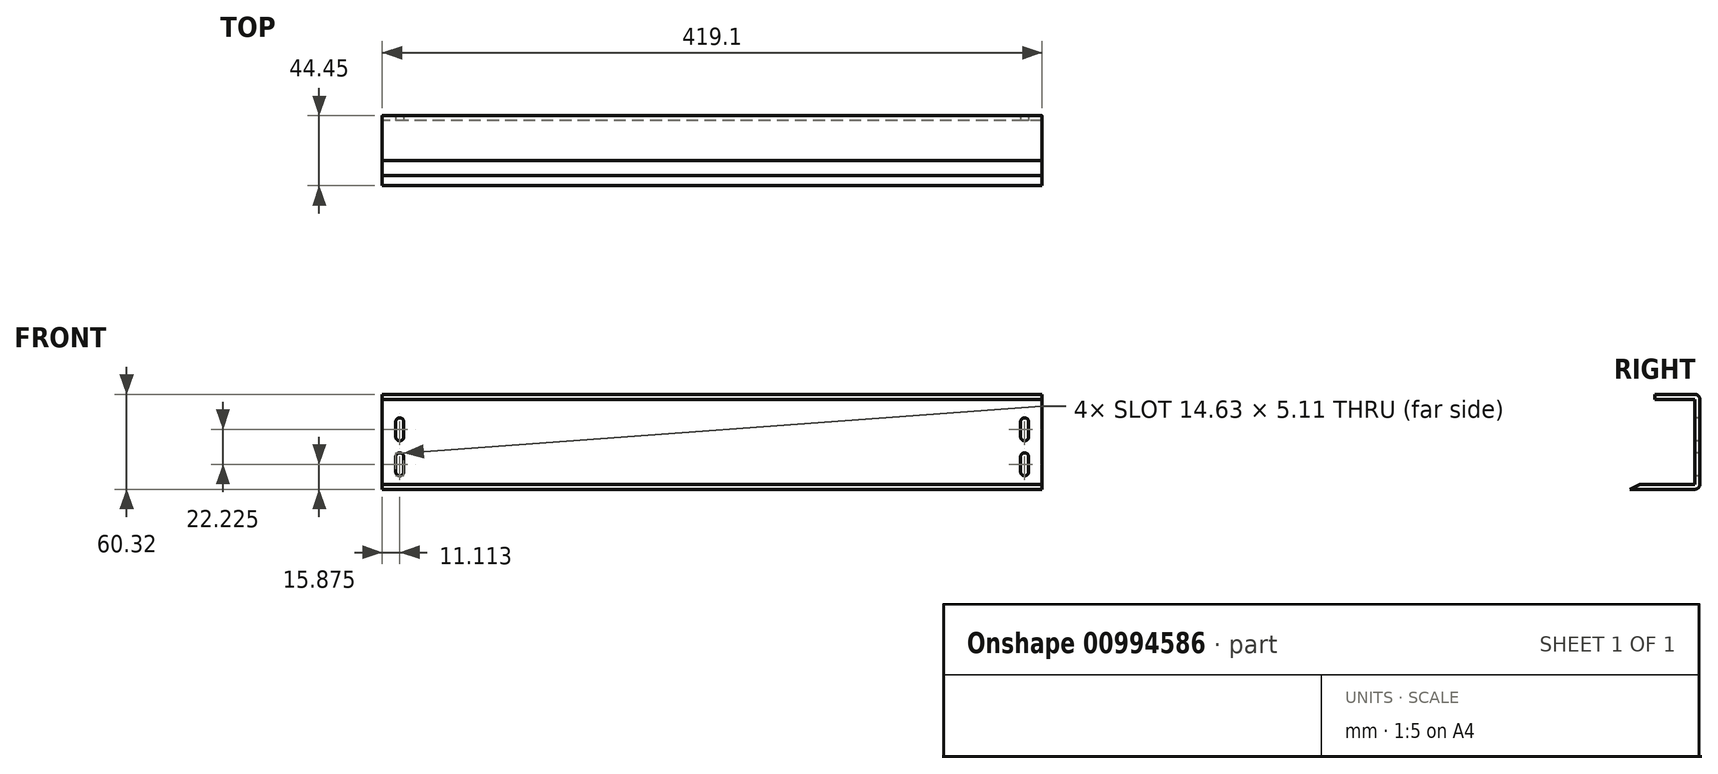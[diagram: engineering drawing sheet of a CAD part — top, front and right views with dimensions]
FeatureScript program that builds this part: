
annotation { "Feature Type Name" : "Feature", "Feature Type Description" : "" }
export const myFeature = defineFeature(function(context is Context, id is Id, definition is map)
    precondition{}
    {
        {
            var Q0;
            Q0=qCreatedBy(makeId("Right.planeOp"),FACE);
            var sketch = newSketch(context, id + "F0", { "sketchPlane" : qUnion([Q0])});
            skLineSegment(sketch, "E0", {"start": v(-44.45, 0) * mm, "end": v(-3.17, 0) * mm});
            skLineSegment(sketch, "E1", {"start": v(0, 3.18) * mm, "end": v(0, 50.8) * mm});
            skLineSegment(sketch, "E2", {"start": v(0, 50.8) * mm, "end": v(-3.18, 50.8) * mm});
            skLineSegment(sketch, "E3", {"start": v(-3.18, 50.8) * mm, "end": v(-3.17, 3.18) * mm});
            skLineSegment(sketch, "E4", {"start": v(-3.18, 3.17) * mm, "end": v(-38.1, 3.17) * mm});
            skLineSegment(sketch, "E5", {"start": v(-38.1, 3.18) * mm, "end": v(-44.45, 0) * mm});
            skLineSegment(sketch, "E6", {"start": v(-38.1, 3.17) * mm, "end": v(-38.1, 0) * mm, "construction": true});
            skPoint(sketch, "E7.visualSharp", {"position": v(0, 0) * mm});
            skArc(sketch, "E7.filletArc", {"start": v(-3.17, 0) * mm, "mid": v(-0.93, 0.93) * mm, "end": v(0, 3.18) * mm});
            skLineSegment(sketch, "E8", {"start": v(-3.18, 50.8) * mm, "end": v(-3.18, 57.15) * mm});
            skLineSegment(sketch, "E9", {"start": v(-3.18, 57.15) * mm, "end": v(-28.58, 57.15) * mm});
            skLineSegment(sketch, "E10", {"start": v(-28.58, 57.15) * mm, "end": v(-28.58, 60.33) * mm});
            skLineSegment(sketch, "E11", {"start": v(-28.58, 60.33) * mm, "end": v(-3.17, 60.33) * mm});
            skLineSegment(sketch, "E12", {"start": v(0, 57.15) * mm, "end": v(0, 50.8) * mm});
            skPoint(sketch, "E13.visualSharp", {"position": v(0, 60.33) * mm});
            skArc(sketch, "E13.filletArc", {"start": v(0, 57.15) * mm, "mid": v(-0.93, 59.4) * mm, "end": v(-3.18, 60.33) * mm});
            skSolve(sketch);
        }
        {
            var Q0;
            Q0=makeQuery(id+"F0.imprint","IMPRINT",FACE,{"disambiguationData":[TD([[makeQuery(id+"F0.imprint","IMPRINT",EDGE,{"derivedFrom":sQuery(id+"F0.wireOp",EDGE,"E0")}),1.0]])]});
            var Q1;
            Q1=makeQuery(id+"F0.imprint","IMPRINT",FACE,{"disambiguationData":[TD([[makeQuery(id+"F0.imprint","IMPRINT",EDGE,{"derivedFrom":sQuery(id+"F0.wireOp",EDGE,"E2")}),-1.0]])]});
            extrude(context, id + "F1", {"entities" : qUnion([Q0, Q1]), "depth" : 419.1 * mm, "offsetDistance" : 25.4 * mm});
        }
        {
            var Q0;
            Q0=makeQuery(id+"F1.opExtrude","SWEPT_FACE",FACE,{"disambiguationData":[OSD([sQuery(id+"F0.wireOp",EDGE,"E3")])]});
            var sketch = newSketch(context, id + "F2", { "sketchPlane" : qUnion([Q0])});
            skLineSegment(sketch, "E14", {"start": v(209.55, 3.18) * mm, "end": v(209.55, 0) * mm, "construction": true});
            skPoint(sketch, "E14.endSnap0", {"position": v(209.55, 3.18) * mm});
            skLineSegment(sketch, "E15", {"start": v(11.11, 3.18) * mm, "end": v(11.11, 3.18) * mm});
            skLineSegment(sketch, "E16.bottom", {"start": v(13.67, 33.34) * mm, "end": v(8.56, 33.34) * mm, "construction": true});
            skLineSegment(sketch, "E16.top", {"start": v(13.67, 42.86) * mm, "end": v(8.56, 42.86) * mm, "construction": true});
            skLineSegment(sketch, "E16.left", {"start": v(13.67, 33.34) * mm, "end": v(13.67, 42.86) * mm});
            skLineSegment(sketch, "E16.right", {"start": v(8.56, 33.34) * mm, "end": v(8.56, 42.86) * mm});
            skPoint(sketch, "E16.middle", {"position": v(11.11, 38.1) * mm});
            skArc(sketch, "E17", {"start": v(8.56, 33.34) * mm, "mid": v(11.11, 30.78) * mm, "end": v(13.67, 33.34) * mm});
            skArc(sketch, "E18", {"start": v(8.56, 42.86) * mm, "mid": v(11.11, 45.42) * mm, "end": v(13.67, 42.86) * mm});
            skLineSegment(sketch, "E19", {"start": v(0, 50.8) * mm, "end": v(0, 3.18) * mm});
            skLineSegment(sketch, "E20", {"start": v(0, 26.99) * mm, "end": v(48.38, 26.99) * mm, "construction": true});
            skLineSegment(sketch, "E21.MirrorCS", {"start": v(13.67, 11.11) * mm, "end": v(8.56, 11.11) * mm, "construction": true});
            skLineSegment(sketch, "E22.MirrorCS", {"start": v(13.67, 20.64) * mm, "end": v(8.56, 20.64) * mm, "construction": true});
            skLineSegment(sketch, "E23.MirrorCS", {"start": v(8.56, 20.64) * mm, "end": v(8.56, 11.11) * mm});
            skLineSegment(sketch, "E24.MirrorCS", {"start": v(13.67, 20.64) * mm, "end": v(13.67, 11.11) * mm});
            skArc(sketch, "E25.MirrorCS", {"start": v(8.56, 20.64) * mm, "mid": v(11.11, 23.2) * mm, "end": v(13.67, 20.64) * mm});
            skPoint(sketch, "E26.MirrorP", {"position": v(11.11, 15.88) * mm});
            skArc(sketch, "E27.MirrorCS", {"start": v(8.56, 11.11) * mm, "mid": v(11.11, 8.56) * mm, "end": v(13.67, 11.11) * mm});
            skLineSegment(sketch, "E28", {"start": v(209.55, 3.18) * mm, "end": v(209.55, 51.7) * mm, "construction": true});
            skLineSegment(sketch, "E29.MirrorCS", {"start": v(405.43, 33.34) * mm, "end": v(405.43, 42.86) * mm});
            skLineSegment(sketch, "E30.MirrorCS", {"start": v(410.54, 33.34) * mm, "end": v(410.54, 42.86) * mm});
            skLineSegment(sketch, "E31.MirrorCS", {"start": v(405.43, 42.86) * mm, "end": v(410.54, 42.86) * mm, "construction": true});
            skLineSegment(sketch, "E32.MirrorCS", {"start": v(405.43, 11.11) * mm, "end": v(410.54, 11.11) * mm, "construction": true});
            skArc(sketch, "E33.MirrorCS", {"start": v(410.54, 11.11) * mm, "mid": v(407.99, 8.56) * mm, "end": v(405.43, 11.11) * mm});
            skLineSegment(sketch, "E34.MirrorCS", {"start": v(405.43, 20.64) * mm, "end": v(405.43, 11.11) * mm});
            skArc(sketch, "E35.MirrorCS", {"start": v(410.54, 33.34) * mm, "mid": v(407.99, 30.78) * mm, "end": v(405.43, 33.34) * mm});
            skLineSegment(sketch, "E36.MirrorCS", {"start": v(410.54, 20.64) * mm, "end": v(410.54, 11.11) * mm});
            skArc(sketch, "E37.MirrorCS", {"start": v(410.54, 42.86) * mm, "mid": v(407.99, 45.42) * mm, "end": v(405.43, 42.86) * mm});
            skLineSegment(sketch, "E38.MirrorCS", {"start": v(405.43, 33.34) * mm, "end": v(410.54, 33.34) * mm, "construction": true});
            skArc(sketch, "E39.MirrorCS", {"start": v(410.54, 20.64) * mm, "mid": v(407.99, 23.2) * mm, "end": v(405.43, 20.64) * mm});
            skLineSegment(sketch, "E40.MirrorCS", {"start": v(405.43, 20.64) * mm, "end": v(410.54, 20.64) * mm, "construction": true});
            skPoint(sketch, "E41.MirrorP", {"position": v(407.99, 15.88) * mm});
            skPoint(sketch, "E42.MirrorP", {"position": v(407.99, 38.1) * mm});
            skLineSegment(sketch, "E43.MirrorCS", {"start": v(419.1, 26.99) * mm, "end": v(370.72, 26.99) * mm, "construction": true});
            skLineSegment(sketch, "E44.MirrorCS", {"start": v(407.99, 3.18) * mm, "end": v(407.99, 3.18) * mm});
            skLineSegment(sketch, "E45.MirrorCS", {"start": v(419.1, 50.8) * mm, "end": v(419.1, 3.18) * mm});
            skSolve(sketch);
        }
        {
            var Q0;
            Q0 = qSketchRegion(id + "F2", true);
            extrude(context, id + "F3", {"entities" : qUnion([Q0]), "operationType" : NewBodyOperationType.REMOVE, "endBound" : BoundingType.THROUGH_ALL, "oppositeDirection" : true, "depth" : 25.4 * mm, "offsetDistance" : 25.4 * mm});
        }
    });
